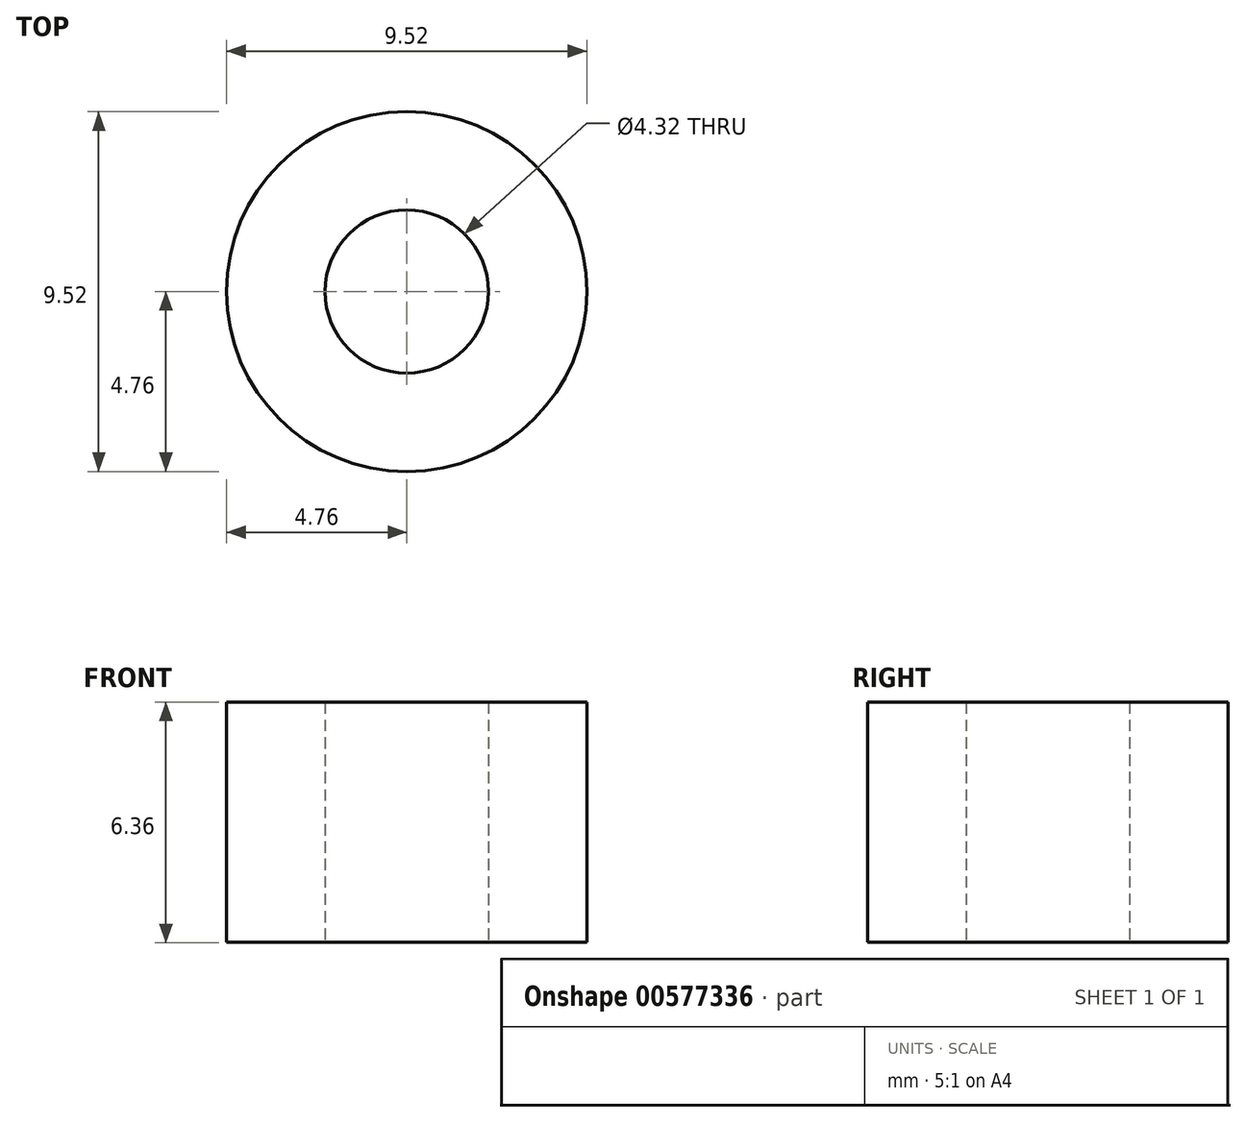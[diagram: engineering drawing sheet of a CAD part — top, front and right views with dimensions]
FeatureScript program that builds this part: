
annotation { "Feature Type Name" : "Feature", "Feature Type Description" : "" }
export const myFeature = defineFeature(function(context is Context, id is Id, definition is map)
    precondition{}
    {
        {
            var Q0;
            Q0=qCreatedBy(makeId("Top.planeOp"),FACE);
            var sketch = newSketch(context, id + "F0", { "sketchPlane" : qUnion([Q0])});
            skCircle(sketch, "E0", {"center": v(0, 0) * mm, "radius": 4.76 * mm});
            skCircle(sketch, "E1", {"center": v(0, 0) * mm, "radius": 2.16 * mm});
            skSolve(sketch);
        }
        {
            var Q0;
            Q0 = qSketchRegion(id + "F0", true);
            extrude(context, id + "F1", {"entities" : qUnion([Q0]), "endBound" : BoundingType.SYMMETRIC, "depth" : 6.35 * mm, "offsetDistance" : 25.4 * mm});
        }
    });
